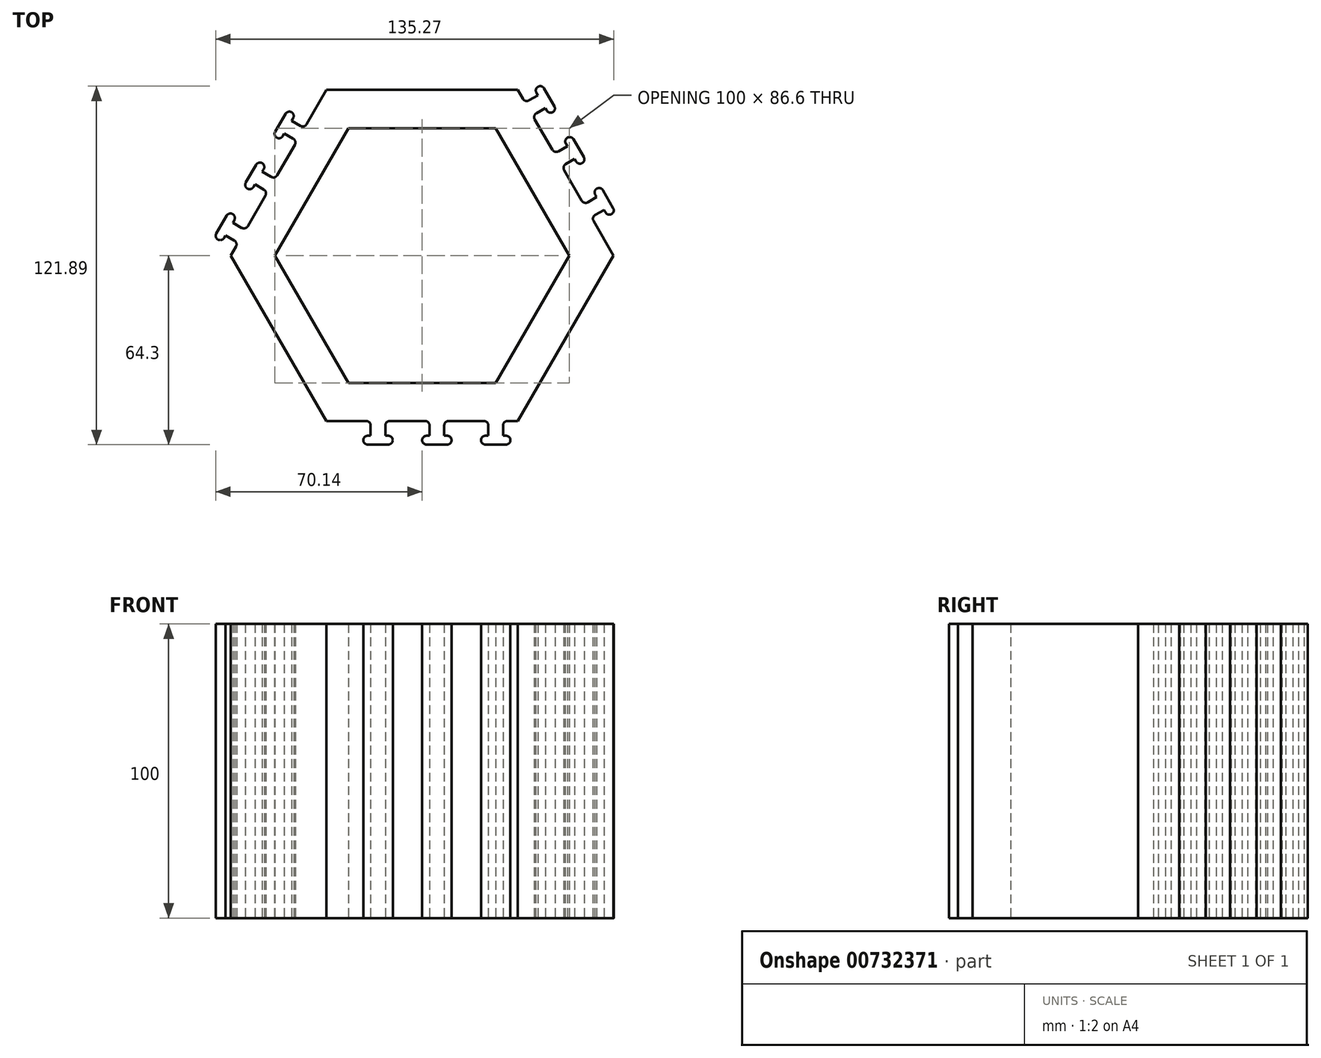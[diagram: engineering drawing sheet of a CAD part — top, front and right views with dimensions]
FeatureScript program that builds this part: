
annotation { "Feature Type Name" : "Feature", "Feature Type Description" : "" }
export const myFeature = defineFeature(function(context is Context, id is Id, definition is map)
    precondition{}
    {
        {
            var Q0;
            Q0=qCreatedBy(makeId("Top.planeOp"),FACE);
            var sketch = newSketch(context, id + "F0", { "sketchPlane" : qUnion([Q0])});
            skLineSegment(sketch, "E0", {"start": v(-25, 43.3) * mm, "end": v(25, 43.3) * mm});
            skLineSegment(sketch, "E1", {"start": v(25, 43.3) * mm, "end": v(50, 0) * mm});
            skLineSegment(sketch, "E2", {"start": v(50, 0) * mm, "end": v(25, -43.3) * mm});
            skLineSegment(sketch, "E3", {"start": v(25, -43.3) * mm, "end": v(-25, -43.3) * mm});
            skLineSegment(sketch, "E4", {"start": v(-25, -43.3) * mm, "end": v(-50, 0) * mm});
            skLineSegment(sketch, "E5", {"start": v(-50, 0) * mm, "end": v(-25, 43.3) * mm});
            skLineSegment(sketch, "E6", {"start": v(0, 0) * mm, "end": v(50, 0) * mm, "construction": true});
            skLineSegment(sketch, "E7", {"start": v(0, 0) * mm, "end": v(-50, 0) * mm, "construction": true});
            skLineSegment(sketch, "E8.0", {"start": v(-65.01, 0) * mm, "end": v(-32.5, 56.3) * mm});
            skLineSegment(sketch, "E8.1", {"start": v(38.26, 46.34) * mm, "end": v(65.01, 0) * mm});
            skLineSegment(sketch, "E8.2", {"start": v(65.01, 0) * mm, "end": v(32.5, -56.3) * mm});
            skLineSegment(sketch, "E8.3", {"start": v(-32.5, 56.3) * mm, "end": v(32.5, 56.3) * mm});
            skLineSegment(sketch, "E8.4", {"start": v(32.5, -56.3) * mm, "end": v(-32.5, -56.3) * mm});
            skLineSegment(sketch, "E8.5", {"start": v(-32.5, -56.3) * mm, "end": v(-65.01, 0) * mm});
            skLineSegment(sketch, "E9", {"start": v(36.3, 52.72) * mm, "end": v(39.34, 54.47) * mm});
            skLineSegment(sketch, "E10", {"start": v(39.34, 54.47) * mm, "end": v(38.84, 55.34) * mm});
            skLineSegment(sketch, "E11", {"start": v(39.38, 57.39) * mm, "end": v(39.38, 57.39) * mm});
            skLineSegment(sketch, "E12", {"start": v(41.43, 56.84) * mm, "end": v(44.93, 50.77) * mm});
            skLineSegment(sketch, "E13", {"start": v(44.38, 48.73) * mm, "end": v(44.38, 48.73) * mm});
            skLineSegment(sketch, "E14", {"start": v(42.34, 49.27) * mm, "end": v(41.84, 50.14) * mm});
            skLineSegment(sketch, "E15", {"start": v(41.84, 50.14) * mm, "end": v(38.8, 48.4) * mm});
            skPoint(sketch, "E16.visualSharp", {"position": v(40.68, 58.14) * mm});
            skArc(sketch, "E16.filletArc", {"start": v(41.43, 56.84) * mm, "mid": v(40.52, 57.54) * mm, "end": v(39.38, 57.39) * mm});
            skPoint(sketch, "E17.visualSharp", {"position": v(45.68, 49.48) * mm});
            skArc(sketch, "E17.filletArc", {"start": v(44.38, 48.73) * mm, "mid": v(45.08, 49.64) * mm, "end": v(44.93, 50.77) * mm});
            skPoint(sketch, "E18.visualSharp", {"position": v(43.09, 47.98) * mm});
            skArc(sketch, "E18.filletArc", {"start": v(42.34, 49.27) * mm, "mid": v(43.25, 48.58) * mm, "end": v(44.38, 48.73) * mm});
            skPoint(sketch, "E19.visualSharp", {"position": v(38.09, 56.64) * mm});
            skArc(sketch, "E19.filletArc", {"start": v(39.38, 57.39) * mm, "mid": v(38.69, 56.48) * mm, "end": v(38.84, 55.34) * mm});
            skArc(sketch, "E20.filletArc", {"start": v(38.8, 48.4) * mm, "mid": v(38.1, 47.48) * mm, "end": v(38.26, 46.34) * mm});
            skLineSegment(sketch, "E21", {"start": v(32.5, 56.3) * mm, "end": v(34.26, 53.27) * mm});
            skPoint(sketch, "E22.visualSharp", {"position": v(35, 51.97) * mm});
            skArc(sketch, "E22.filletArc", {"start": v(34.26, 53.27) * mm, "mid": v(35.17, 52.57) * mm, "end": v(36.3, 52.72) * mm});
            skArc(sketch, "E23.1.0.0", {"start": v(48.8, 31.07) * mm, "mid": v(48.1, 30.16) * mm, "end": v(48.26, 29.02) * mm});
            skLineSegment(sketch, "E23.1.0.1", {"start": v(51.84, 32.82) * mm, "end": v(48.8, 31.07) * mm});
            skArc(sketch, "E23.1.0.2", {"start": v(52.34, 31.95) * mm, "mid": v(53.25, 31.26) * mm, "end": v(54.38, 31.4) * mm});
            skLineSegment(sketch, "E23.1.0.3", {"start": v(52.34, 31.95) * mm, "end": v(51.84, 32.82) * mm});
            skArc(sketch, "E23.1.0.4", {"start": v(54.38, 31.4) * mm, "mid": v(55.08, 32.32) * mm, "end": v(54.93, 33.45) * mm});
            skLineSegment(sketch, "E23.1.0.5", {"start": v(51.43, 39.52) * mm, "end": v(54.93, 33.45) * mm});
            skArc(sketch, "E23.1.0.6", {"start": v(51.43, 39.52) * mm, "mid": v(50.52, 40.22) * mm, "end": v(49.38, 40.07) * mm});
            skArc(sketch, "E23.1.0.7", {"start": v(49.38, 40.07) * mm, "mid": v(48.69, 39.15) * mm, "end": v(48.84, 38.02) * mm});
            skLineSegment(sketch, "E23.1.0.8", {"start": v(49.34, 37.15) * mm, "end": v(48.84, 38.02) * mm});
            skLineSegment(sketch, "E23.1.0.9", {"start": v(46.3, 35.4) * mm, "end": v(49.34, 37.15) * mm});
            skArc(sketch, "E23.1.0.10", {"start": v(44.26, 35.95) * mm, "mid": v(45.17, 35.25) * mm, "end": v(46.3, 35.4) * mm});
            skArc(sketch, "E23.2.0.0", {"start": v(58.8, 13.75) * mm, "mid": v(58.1, 12.84) * mm, "end": v(58.26, 11.7) * mm});
            skLineSegment(sketch, "E23.2.0.1", {"start": v(61.84, 15.5) * mm, "end": v(58.8, 13.75) * mm});
            skArc(sketch, "E23.2.0.2", {"start": v(62.34, 14.63) * mm, "mid": v(63.25, 13.94) * mm, "end": v(64.38, 14.08) * mm});
            skLineSegment(sketch, "E23.2.0.3", {"start": v(62.34, 14.63) * mm, "end": v(61.84, 15.5) * mm});
            skArc(sketch, "E23.2.0.4", {"start": v(64.38, 14.08) * mm, "mid": v(65.08, 15) * mm, "end": v(64.93, 16.13) * mm});
            skLineSegment(sketch, "E23.2.0.5", {"start": v(61.43, 22.2) * mm, "end": v(64.93, 16.13) * mm});
            skArc(sketch, "E23.2.0.6", {"start": v(61.43, 22.2) * mm, "mid": v(60.52, 22.9) * mm, "end": v(59.38, 22.75) * mm});
            skArc(sketch, "E23.2.0.7", {"start": v(59.38, 22.75) * mm, "mid": v(58.69, 21.83) * mm, "end": v(58.84, 20.7) * mm});
            skLineSegment(sketch, "E23.2.0.8", {"start": v(59.34, 19.83) * mm, "end": v(58.84, 20.7) * mm});
            skLineSegment(sketch, "E23.2.0.9", {"start": v(56.3, 18.08) * mm, "end": v(59.34, 19.83) * mm});
            skArc(sketch, "E23.2.0.10", {"start": v(54.26, 18.63) * mm, "mid": v(55.17, 17.93) * mm, "end": v(56.3, 18.08) * mm});
            skLineSegment(sketch, "E23.direction1", {"start": v(39.55, 47.1) * mm, "end": v(49.55, 29.77) * mm, "construction": true});
            skArc(sketch, "E24.1.0", {"start": v(-63.26, 3.03) * mm, "mid": v(-63.11, 4.17) * mm, "end": v(-63.81, 5.08) * mm});
            skArc(sketch, "E24.1.1", {"start": v(-61.31, 9.41) * mm, "mid": v(-60.17, 9.26) * mm, "end": v(-59.26, 9.96) * mm});
            skLineSegment(sketch, "E24.1.2", {"start": v(-64.34, 11.16) * mm, "end": v(-61.31, 9.41) * mm});
            skLineSegment(sketch, "E24.1.3", {"start": v(-63.81, 5.08) * mm, "end": v(-66.84, 6.83) * mm});
            skLineSegment(sketch, "E24.1.4", {"start": v(-63.84, 12.03) * mm, "end": v(-64.34, 11.16) * mm});
            skLineSegment(sketch, "E24.1.5", {"start": v(-66.84, 6.83) * mm, "end": v(-67.34, 5.96) * mm});
            skArc(sketch, "E24.1.6", {"start": v(-69.94, 7.46) * mm, "mid": v(-70.09, 6.33) * mm, "end": v(-69.4, 5.42) * mm});
            skArc(sketch, "E24.1.7", {"start": v(-69.4, 5.42) * mm, "mid": v(-68.25, 5.27) * mm, "end": v(-67.34, 5.96) * mm});
            skLineSegment(sketch, "E24.1.8", {"start": v(-69.94, 7.46) * mm, "end": v(-66.44, 13.53) * mm});
            skArc(sketch, "E24.1.9", {"start": v(-64.4, 14.08) * mm, "mid": v(-65.53, 14.23) * mm, "end": v(-66.44, 13.53) * mm});
            skArc(sketch, "E24.1.10", {"start": v(-63.84, 12.03) * mm, "mid": v(-63.7, 13.16) * mm, "end": v(-64.4, 14.08) * mm});
            skLineSegment(sketch, "E24.1.11", {"start": v(-53.81, 22.4) * mm, "end": v(-56.84, 24.15) * mm});
            skArc(sketch, "E24.1.12", {"start": v(-53.26, 20.35) * mm, "mid": v(-53.11, 21.49) * mm, "end": v(-53.81, 22.4) * mm});
            skLineSegment(sketch, "E24.1.13", {"start": v(-56.84, 24.15) * mm, "end": v(-57.34, 23.28) * mm});
            skArc(sketch, "E24.1.14", {"start": v(-59.4, 22.74) * mm, "mid": v(-58.25, 22.59) * mm, "end": v(-57.34, 23.28) * mm});
            skArc(sketch, "E24.1.15", {"start": v(-59.94, 24.78) * mm, "mid": v(-60.09, 23.65) * mm, "end": v(-59.4, 22.74) * mm});
            skLineSegment(sketch, "E24.1.16", {"start": v(-59.94, 24.78) * mm, "end": v(-56.44, 30.85) * mm});
            skArc(sketch, "E24.1.17", {"start": v(-54.4, 31.4) * mm, "mid": v(-55.53, 31.55) * mm, "end": v(-56.44, 30.85) * mm});
            skArc(sketch, "E24.1.18", {"start": v(-53.84, 29.35) * mm, "mid": v(-53.7, 30.49) * mm, "end": v(-54.4, 31.4) * mm});
            skLineSegment(sketch, "E24.1.19", {"start": v(-53.84, 29.35) * mm, "end": v(-54.34, 28.48) * mm});
            skLineSegment(sketch, "E24.1.20", {"start": v(-54.34, 28.48) * mm, "end": v(-51.31, 26.73) * mm});
            skArc(sketch, "E24.1.21", {"start": v(-51.31, 26.73) * mm, "mid": v(-50.17, 26.58) * mm, "end": v(-49.26, 27.28) * mm});
            skArc(sketch, "E24.1.22", {"start": v(-43.26, 37.67) * mm, "mid": v(-43.11, 38.81) * mm, "end": v(-43.81, 39.72) * mm});
            skLineSegment(sketch, "E24.1.23", {"start": v(-43.81, 39.72) * mm, "end": v(-46.84, 41.47) * mm});
            skArc(sketch, "E24.1.24", {"start": v(-41.31, 44.05) * mm, "mid": v(-40.17, 43.9) * mm, "end": v(-39.26, 44.6) * mm});
            skLineSegment(sketch, "E24.1.25", {"start": v(-44.34, 45.8) * mm, "end": v(-41.31, 44.05) * mm});
            skLineSegment(sketch, "E24.1.26", {"start": v(-43.84, 46.67) * mm, "end": v(-44.34, 45.8) * mm});
            skLineSegment(sketch, "E24.1.27", {"start": v(-46.84, 41.47) * mm, "end": v(-47.34, 40.6) * mm});
            skArc(sketch, "E24.1.28", {"start": v(-49.4, 40.06) * mm, "mid": v(-48.25, 39.9) * mm, "end": v(-47.34, 40.6) * mm});
            skArc(sketch, "E24.1.29", {"start": v(-43.84, 46.67) * mm, "mid": v(-43.7, 47.8) * mm, "end": v(-44.4, 48.72) * mm});
            skArc(sketch, "E24.1.30", {"start": v(-49.94, 42.1) * mm, "mid": v(-50.09, 40.97) * mm, "end": v(-49.4, 40.06) * mm});
            skArc(sketch, "E24.1.31", {"start": v(-44.4, 48.72) * mm, "mid": v(-45.53, 48.87) * mm, "end": v(-46.44, 48.17) * mm});
            skLineSegment(sketch, "E24.1.32", {"start": v(-49.94, 42.1) * mm, "end": v(-46.44, 48.17) * mm});
            skArc(sketch, "E24.2.0", {"start": v(29, -56.3) * mm, "mid": v(27.94, -56.74) * mm, "end": v(27.5, -57.8) * mm});
            skArc(sketch, "E24.2.1", {"start": v(22.5, -57.8) * mm, "mid": v(22.07, -56.74) * mm, "end": v(21, -56.3) * mm});
            skLineSegment(sketch, "E24.2.2", {"start": v(22.5, -61.3) * mm, "end": v(22.5, -57.8) * mm});
            skLineSegment(sketch, "E24.2.3", {"start": v(27.5, -57.8) * mm, "end": v(27.5, -61.3) * mm});
            skLineSegment(sketch, "E24.2.4", {"start": v(21.5, -61.3) * mm, "end": v(22.5, -61.3) * mm});
            skLineSegment(sketch, "E24.2.5", {"start": v(27.5, -61.3) * mm, "end": v(28.5, -61.3) * mm});
            skArc(sketch, "E24.2.6", {"start": v(28.5, -64.3) * mm, "mid": v(29.57, -63.86) * mm, "end": v(30, -62.8) * mm});
            skArc(sketch, "E24.2.7", {"start": v(30, -62.8) * mm, "mid": v(29.57, -61.74) * mm, "end": v(28.5, -61.3) * mm});
            skLineSegment(sketch, "E24.2.8", {"start": v(28.5, -64.3) * mm, "end": v(21.5, -64.3) * mm});
            skArc(sketch, "E24.2.9", {"start": v(20, -62.8) * mm, "mid": v(20.44, -63.86) * mm, "end": v(21.5, -64.3) * mm});
            skArc(sketch, "E24.2.10", {"start": v(21.5, -61.3) * mm, "mid": v(20.44, -61.74) * mm, "end": v(20, -62.8) * mm});
            skLineSegment(sketch, "E24.2.11", {"start": v(7.5, -57.8) * mm, "end": v(7.5, -61.3) * mm});
            skArc(sketch, "E24.2.12", {"start": v(9, -56.3) * mm, "mid": v(7.94, -56.74) * mm, "end": v(7.5, -57.8) * mm});
            skLineSegment(sketch, "E24.2.13", {"start": v(7.5, -61.3) * mm, "end": v(8.5, -61.3) * mm});
            skArc(sketch, "E24.2.14", {"start": v(10, -62.8) * mm, "mid": v(9.57, -61.74) * mm, "end": v(8.5, -61.3) * mm});
            skArc(sketch, "E24.2.15", {"start": v(8.5, -64.3) * mm, "mid": v(9.57, -63.86) * mm, "end": v(10, -62.8) * mm});
            skLineSegment(sketch, "E24.2.16", {"start": v(8.5, -64.3) * mm, "end": v(1.5, -64.3) * mm});
            skArc(sketch, "E24.2.17", {"start": v(0, -62.8) * mm, "mid": v(0.44, -63.86) * mm, "end": v(1.5, -64.3) * mm});
            skArc(sketch, "E24.2.18", {"start": v(1.5, -61.3) * mm, "mid": v(0.44, -61.74) * mm, "end": v(0, -62.8) * mm});
            skLineSegment(sketch, "E24.2.19", {"start": v(1.5, -61.3) * mm, "end": v(2.5, -61.3) * mm});
            skLineSegment(sketch, "E24.2.20", {"start": v(2.5, -61.3) * mm, "end": v(2.5, -57.8) * mm});
            skArc(sketch, "E24.2.21", {"start": v(2.5, -57.8) * mm, "mid": v(2.07, -56.74) * mm, "end": v(1, -56.3) * mm});
            skArc(sketch, "E24.2.22", {"start": v(-11, -56.3) * mm, "mid": v(-12.06, -56.74) * mm, "end": v(-12.5, -57.8) * mm});
            skLineSegment(sketch, "E24.2.23", {"start": v(-12.5, -57.8) * mm, "end": v(-12.5, -61.3) * mm});
            skArc(sketch, "E24.2.24", {"start": v(-17.5, -57.8) * mm, "mid": v(-17.93, -56.74) * mm, "end": v(-19, -56.3) * mm});
            skLineSegment(sketch, "E24.2.25", {"start": v(-17.5, -61.3) * mm, "end": v(-17.5, -57.8) * mm});
            skLineSegment(sketch, "E24.2.26", {"start": v(-18.5, -61.3) * mm, "end": v(-17.5, -61.3) * mm});
            skLineSegment(sketch, "E24.2.27", {"start": v(-12.5, -61.3) * mm, "end": v(-11.5, -61.3) * mm});
            skArc(sketch, "E24.2.28", {"start": v(-10, -62.8) * mm, "mid": v(-10.43, -61.74) * mm, "end": v(-11.5, -61.3) * mm});
            skArc(sketch, "E24.2.29", {"start": v(-18.5, -61.3) * mm, "mid": v(-19.56, -61.74) * mm, "end": v(-20, -62.8) * mm});
            skArc(sketch, "E24.2.30", {"start": v(-11.5, -64.3) * mm, "mid": v(-10.43, -63.86) * mm, "end": v(-10, -62.8) * mm});
            skArc(sketch, "E24.2.31", {"start": v(-20, -62.8) * mm, "mid": v(-19.56, -63.86) * mm, "end": v(-18.5, -64.3) * mm});
            skLineSegment(sketch, "E24.2.32", {"start": v(-11.5, -64.3) * mm, "end": v(-18.5, -64.3) * mm});
            skPoint(sketch, "E24.center", {"position": v(0, 0) * mm});
            skSolve(sketch);
        }
        {
            var Q0;
            Q0 = qSketchRegion(id + "F0", true);
            extrude(context, id + "F1", {"entities" : qUnion([Q0]), "depth" : 100 * mm, "offsetDistance" : 25 * mm});
        }
    });
